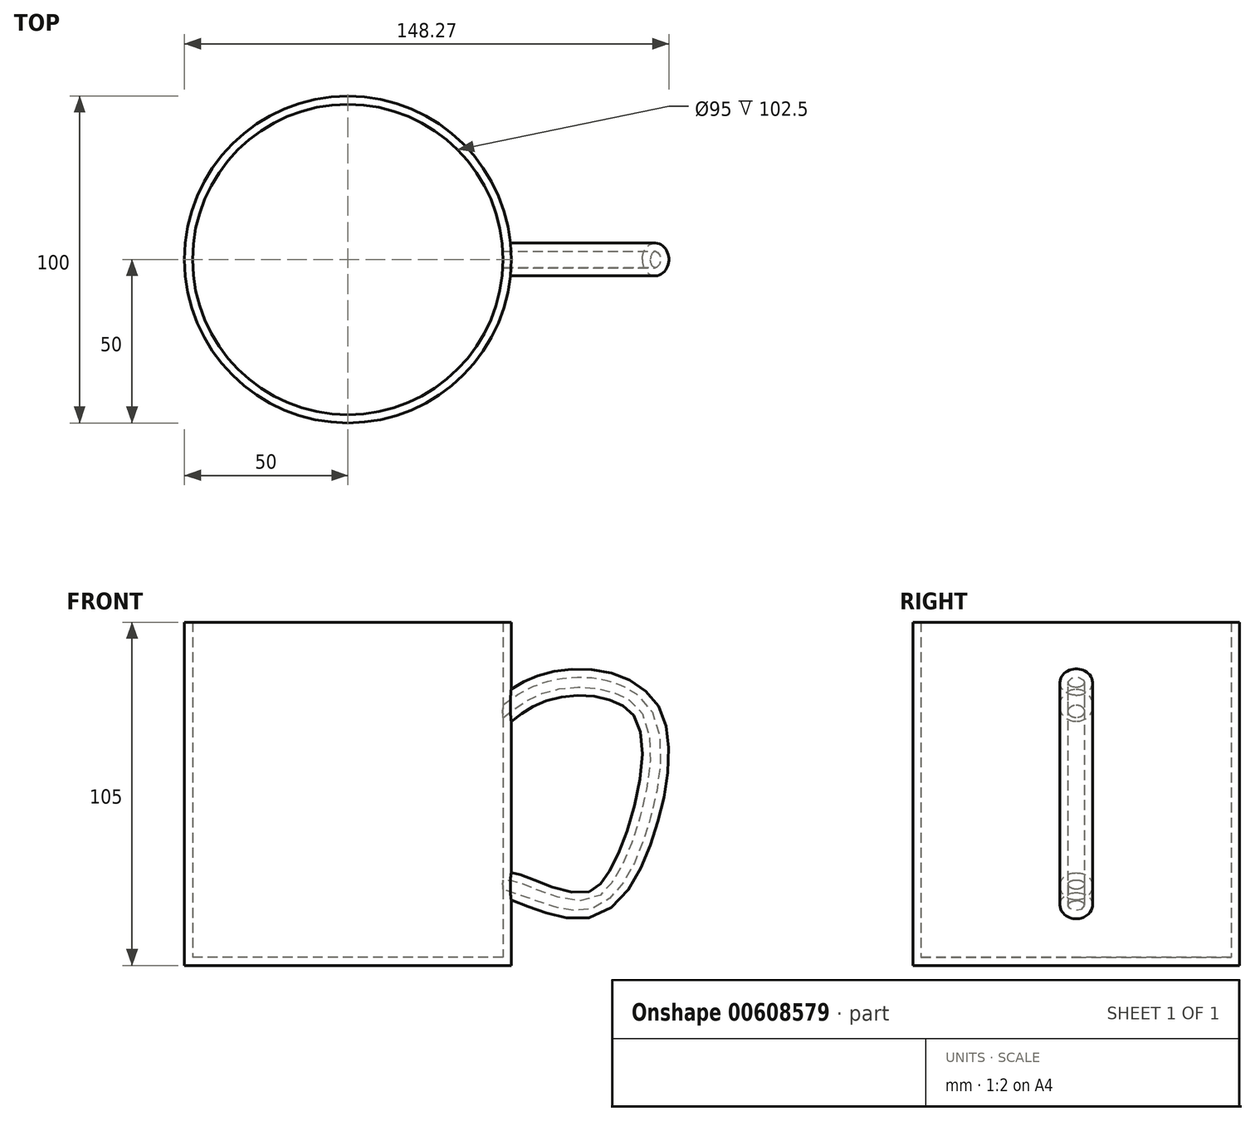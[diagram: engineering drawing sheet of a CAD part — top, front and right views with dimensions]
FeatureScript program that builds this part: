
annotation { "Feature Type Name" : "Feature", "Feature Type Description" : "" }
export const myFeature = defineFeature(function(context is Context, id is Id, definition is map)
    precondition{}
    {
        {
            var Q0;
            Q0=qCreatedBy(makeId("Top.planeOp"),FACE);
            var sketch = newSketch(context, id + "F0", { "sketchPlane" : qUnion([Q0])});
            skCircle(sketch, "E0", {"center": v(0, 0) * mm, "radius": 50 * mm});
            skSolve(sketch);
        }
        {
            var Q0;
            Q0 = qSketchRegion(id + "F0", true);
            extrude(context, id + "F1", {"entities" : qUnion([Q0]), "depth" : 105 * mm, "offsetDistance" : 25 * mm});
        }
        {
            var Q0;
            Q0=qCreatedBy(makeId("Front.planeOp"),FACE);
            var sketch = newSketch(context, id + "F2", { "sketchPlane" : qUnion([Q0])});
            skFitSpline(sketch, "E1", {"points": [v(46.88, 78.41) * mm, v(57.4, 84.86) * mm, v(75.04, 87.23) * mm, v(92.34, 77.4) * mm, v(91.32, 43.13) * mm, v(74.02, 18.03) * mm, v(51.63, 22.78) * mm, v(44.5, 24.82) * mm, v(38.4, 27.87) * mm], "startDerivative": vector(92.15, 68.17) * mm, "endDerivative": vector(-80.27, 45.55) * mm});
            skSolve(sketch);
        }
        {
            var Q0;
            Q0=qCreatedBy(makeId("Right.planeOp"),FACE);
            cPlane(context, id + "F3", {"entities" : qUnion([Q0]), "cplaneType" : CPlaneType.OFFSET, "offset" : 50 * mm, "width" : 150 * mm, "height" : 150 * mm});
        }
        {
            var Q0;
            Q0=qCreatedBy(id+"F3.planeOp",FACE);
            var sketch = newSketch(context, id + "F4", { "sketchPlane" : qUnion([Q0])});
            skCircle(sketch, "E2", {"center": v(0, 79.57) * mm, "radius": 5 * mm});
            skSolve(sketch);
        }
        {
            var Q0;
            Q0=makeQuery(id+"F4.imprint","IMPRINT",FACE,{"disambiguationData":[TD([[makeQuery(id+"F4.imprint","IMPRINT",EDGE,{"derivedFrom":sQuery(id+"F4.wireOp",EDGE,"E2")}),1.0]])]});
            var Q1;
            Q1=sQuery(id+"F2.wireOp",EDGE,"E1");
            sweep(context, id + "F5", {"operationType" : NewBodyOperationType.ADD, "profiles" : qUnion([Q0]), "path" : qUnion([Q1])});
        }
        {
            var Q0;
            Q0=makeQuery(id+"F1.opExtrude","CAP_FACE",FACE,{"disambiguationData":[OSD([sQuery(id+"F0.wireOp",EDGE,"E0")])],"isStart":false});
            shell(context, id + "F6", {"entities" : qUnion([Q0]), "thickness" : 2.5 * mm});
        }
    });
